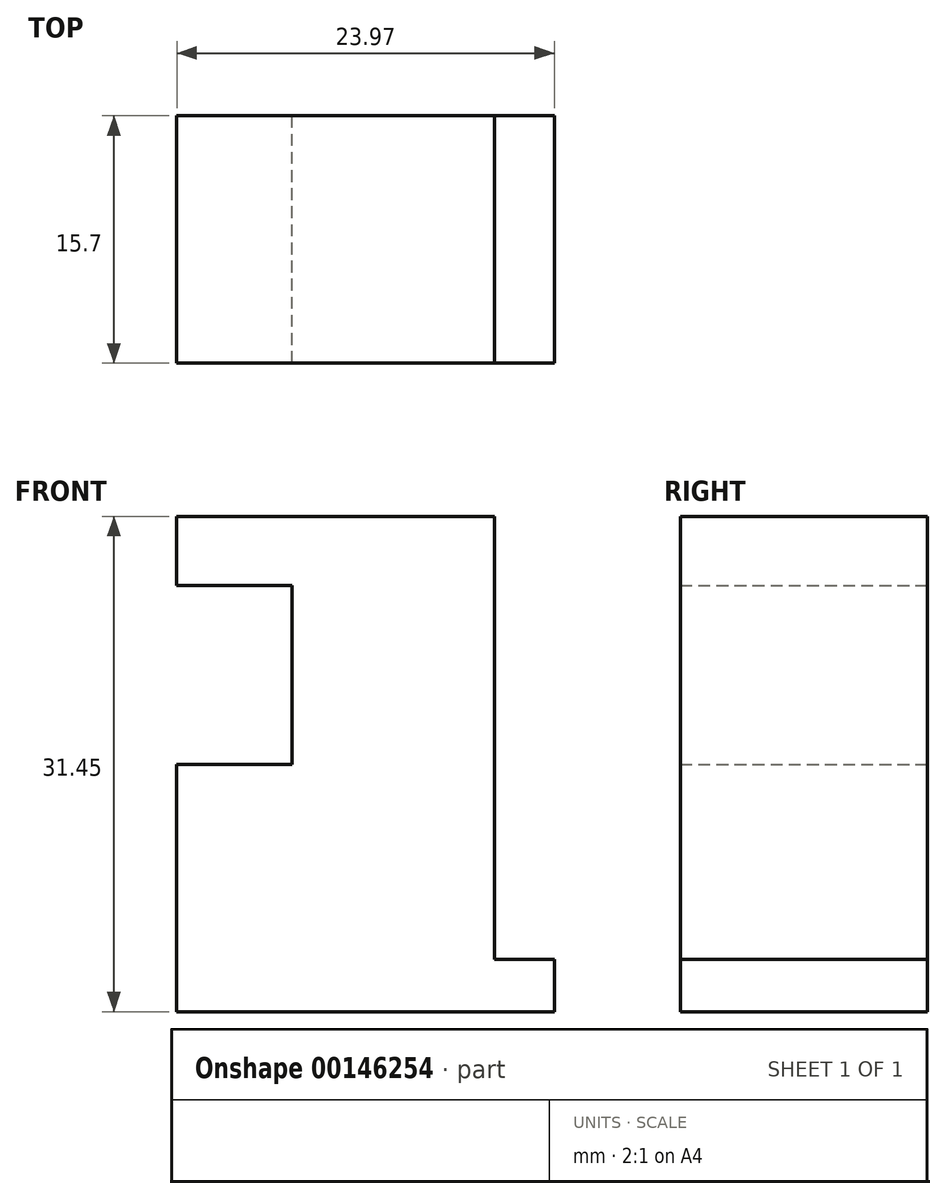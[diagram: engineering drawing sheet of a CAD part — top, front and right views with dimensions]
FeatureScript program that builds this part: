
annotation { "Feature Type Name" : "Feature", "Feature Type Description" : "" }
export const myFeature = defineFeature(function(context is Context, id is Id, definition is map)
    precondition{}
    {
        {
            var Q0;
            Q0=qCreatedBy(makeId("Front.planeOp"),FACE);
            var sketch = newSketch(context, id + "F0", { "sketchPlane" : qUnion([Q0])});
            skLineSegment(sketch, "E0", {"start": v(-23.3, -23.62) * mm, "end": v(-23.3, -7.92) * mm});
            skLineSegment(sketch, "E1", {"start": v(-23.3, -7.92) * mm, "end": v(-15.98, -7.92) * mm});
            skLineSegment(sketch, "E2", {"start": v(-15.98, -7.92) * mm, "end": v(-15.98, 3.46) * mm});
            skLineSegment(sketch, "E3", {"start": v(-15.98, 3.46) * mm, "end": v(-23.3, 3.46) * mm});
            skLineSegment(sketch, "E4", {"start": v(-23.3, 3.46) * mm, "end": v(-23.3, 7.83) * mm});
            skLineSegment(sketch, "E5", {"start": v(-23.3, 7.83) * mm, "end": v(-15.98, 7.83) * mm});
            skLineSegment(sketch, "E6", {"start": v(-15.98, 7.83) * mm, "end": v(-12.92, 7.83) * mm});
            skLineSegment(sketch, "E7", {"start": v(-12.92, 7.83) * mm, "end": v(-3.13, 7.83) * mm});
            skPoint(sketch, "E7.endSnap0", {"position": v(-14.45, 7.83) * mm});
            skLineSegment(sketch, "E8", {"start": v(-3.13, 7.83) * mm, "end": v(-3.13, -20.3) * mm});
            skLineSegment(sketch, "E9", {"start": v(-3.13, -20.3) * mm, "end": v(0.68, -20.3) * mm});
            skLineSegment(sketch, "E10", {"start": v(-23.3, -23.62) * mm, "end": v(0.68, -23.62) * mm});
            skLineSegment(sketch, "E11", {"start": v(0.68, -23.62) * mm, "end": v(0.68, -20.3) * mm});
            skLineSegment(sketch, "E12", {"start": v(-3.13, -20.3) * mm, "end": v(-3.13, -23.62) * mm});
            skSolve(sketch);
        }
        {
            var Q0;
            {var subQ0=sQuery(id+"F0.wireOp",EDGE,"E0");Q0=makeQuery(id+"F0.imprint","IMPRINT",FACE,{"disambiguationData":[TD([[makeQuery(id+"F0.imprint","IMPRINT",EDGE,{"derivedFrom":subQ0}),-1.0]])]});}
            var Q1;
            Q1=makeQuery(id+"F0.imprint","IMPRINT",FACE,{"disambiguationData":[TD([[makeQuery(id+"F0.imprint","IMPRINT",EDGE,{"derivedFrom":sQuery(id+"F0.wireOp",EDGE,"E9")}),-1.0]])]});
            extrude(context, id + "F1", {"entities" : qUnion([Q0, Q1]), "depth" : 15.7 * mm});
        }
    });
